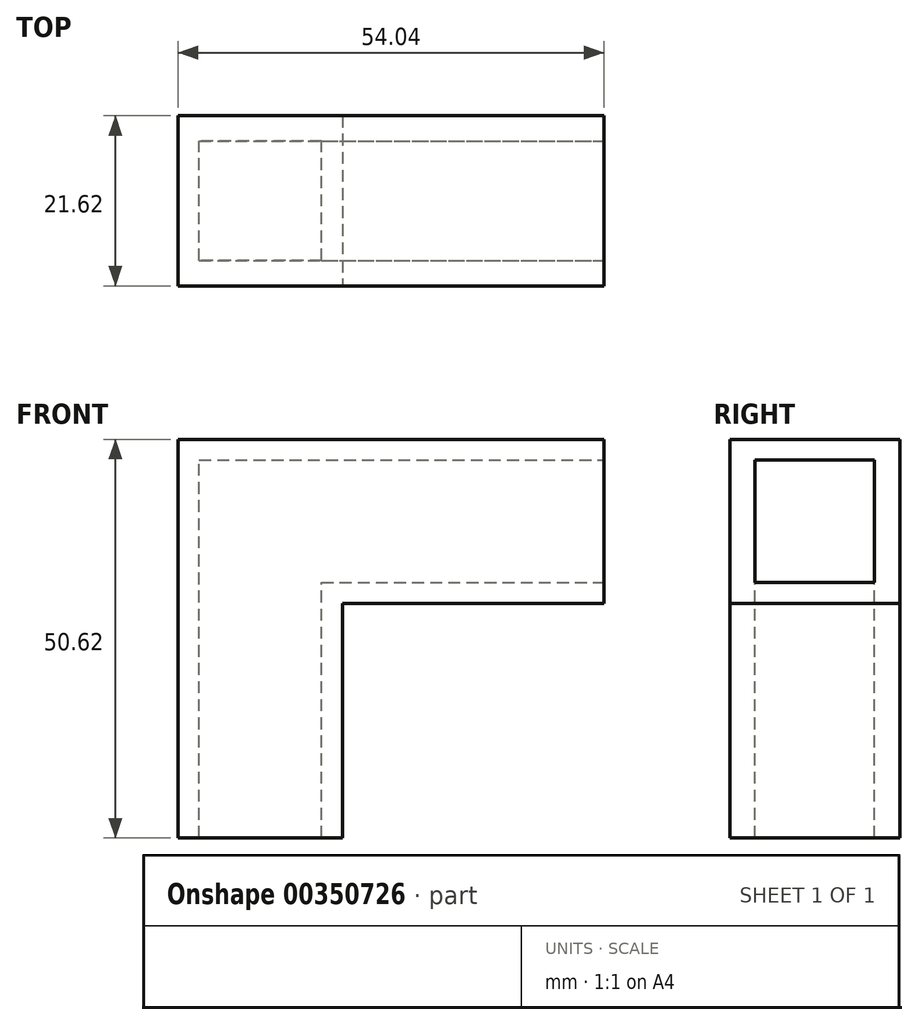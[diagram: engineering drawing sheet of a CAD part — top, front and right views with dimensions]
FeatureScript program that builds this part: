
annotation { "Feature Type Name" : "Feature", "Feature Type Description" : "" }
export const myFeature = defineFeature(function(context is Context, id is Id, definition is map)
    precondition{}
    {
        {
            var Q0;
            Q0=qCreatedBy(makeId("Front.planeOp"),FACE);
            var sketch = newSketch(context, id + "F0", { "sketchPlane" : qUnion([Q0])});
            skLineSegment(sketch, "E0", {"start": v(0, 0) * mm, "end": v(0, 40.2) * mm});
            skLineSegment(sketch, "E1", {"start": v(0, 40.2) * mm, "end": v(43.6, 40.2) * mm});
            skSolve(sketch);
        }
        {
            var Q0;
            Q0=qCreatedBy(makeId("Top.planeOp"),FACE);
            var sketch = newSketch(context, id + "F1", { "sketchPlane" : qUnion([Q0])});
            skLineSegment(sketch, "E2.bottom", {"start": v(10.43, -10.8) * mm, "end": v(-10.43, -10.8) * mm});
            skLineSegment(sketch, "E2.top", {"start": v(10.43, 10.8) * mm, "end": v(-10.43, 10.8) * mm});
            skLineSegment(sketch, "E2.left", {"start": v(10.43, -10.8) * mm, "end": v(10.43, 10.8) * mm});
            skLineSegment(sketch, "E2.right", {"start": v(-10.43, -10.8) * mm, "end": v(-10.43, 10.8) * mm});
            skPoint(sketch, "E2.middle", {"position": v(0, 0) * mm});
            skLineSegment(sketch, "E3.bottom", {"start": v(7.77, -7.58) * mm, "end": v(-7.77, -7.58) * mm});
            skLineSegment(sketch, "E3.top", {"start": v(7.77, 7.58) * mm, "end": v(-7.77, 7.58) * mm});
            skLineSegment(sketch, "E3.left", {"start": v(7.77, -7.58) * mm, "end": v(7.77, 7.58) * mm});
            skLineSegment(sketch, "E3.right", {"start": v(-7.77, -7.58) * mm, "end": v(-7.77, 7.58) * mm});
            skSolve(sketch);
        }
        {
            var Q0;
            Q0=makeQuery(id+"F1.imprint","IMPRINT",FACE,{"disambiguationData":[TD([[makeQuery(id+"F1.imprint","IMPRINT",EDGE,{"derivedFrom":sQuery(id+"F1.wireOp",EDGE,"E2.bottom")}),-1.0]])]});
            var Q1;
            Q1=sQuery(id+"F0.wireOp",EDGE,"E0");
            var Q2;
            Q2=sQuery(id+"F0.wireOp",EDGE,"E1");
            sweep(context, id + "F2", {"profiles" : qUnion([Q0]), "path" : qUnion([Q1, Q2])});
        }
    });
